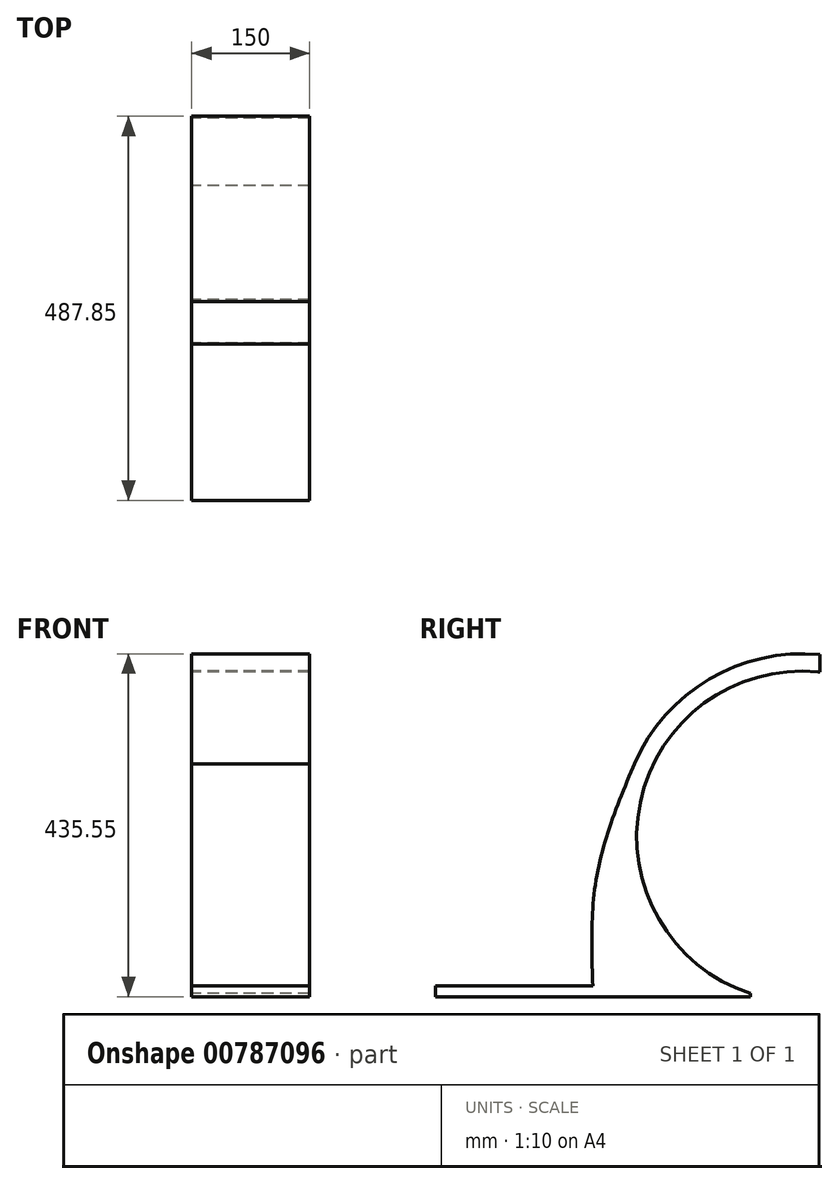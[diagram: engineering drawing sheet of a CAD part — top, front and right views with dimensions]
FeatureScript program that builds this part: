
annotation { "Feature Type Name" : "Feature", "Feature Type Description" : "" }
export const myFeature = defineFeature(function(context is Context, id is Id, definition is map)
    precondition{}
    {
        {
            var Q0;
            Q0=qCreatedBy(makeId("Right.planeOp"),FACE);
            var sketch = newSketch(context, id + "F0", { "sketchPlane" : qUnion([Q0])});
            skLineSegment(sketch, "E0", {"start": v(102.98, 0) * mm, "end": v(-97.02, 0) * mm});
            skLineSegment(sketch, "E1", {"start": v(-35.78, 150) * mm, "end": v(-92.34, 150) * mm});
            skPoint(sketch, "E2.third.point", {"position": v(169.6, 409.55) * mm});
            skArc(sketch, "E3", {"start": v(188.7, 408.56) * mm, "mid": v(-37.24, 242.69) * mm, "end": v(102.98, 0) * mm});
            skArc(sketch, "E4.0", {"start": v(190.83, 430.45) * mm, "mid": v(-52.22, 271.7) * mm, "end": v(50, 0) * mm});
            skFitSpline(sketch, "E5", {"points": [v(-97.02, 0) * mm, v(-92.34, 150) * mm, v(-44.67, 291.64) * mm], "startDerivative": vector(-12.28, 303.75) * mm, "endDerivative": vector(117.44, 279.34) * mm});
            skLineSegment(sketch, "E6", {"start": v(190.83, 430.45) * mm, "end": v(190.83, 408.56) * mm});
            skLineSegment(sketch, "E7", {"start": v(190.83, 408.56) * mm, "end": v(188.7, 408.56) * mm});
            skSolve(sketch);
        }
        {
            var Q0;
            {var subQ0=sQuery(id+"F0.wireOp",EDGE,"E5");var subQ1=sQuery(id+"F0.wireOp",EDGE,"E1");var subQ2=makeQuery(id+"F0.imprint","INTERSECT",VERTEX,{"derivedFrom":[subQ1,subQ0]});Q0=makeQuery(id+"F0.imprint","IMPRINT",FACE,{"disambiguationData":[TD([[makeQuery(id+"F0.imprint","IMPRINT",EDGE,{"disambiguationData":[TD([[subQ2,1.0]])],"derivedFrom":subQ1}),-1.0]])]});}
            var Q1;
            {var subQ0=sQuery(id+"F0.wireOp",EDGE,"E5");var subQ1=sQuery(id+"F0.wireOp",EDGE,"E0");var subQ2=makeQuery(id+"F0.imprint","INTERSECT",VERTEX,{"derivedFrom":[subQ1,subQ0]});Q1=makeQuery(id+"F0.imprint","IMPRINT",FACE,{"disambiguationData":[TD([[makeQuery(id+"F0.imprint","IMPRINT",EDGE,{"disambiguationData":[TD([[subQ2,1.0]])],"derivedFrom":subQ1}),-1.0]])]});}
            var Q2;
            {var subQ5=sQuery(id+"F0.wireOp",EDGE,"E6");Q2=makeQuery(id+"F0.imprint","IMPRINT",FACE,{"disambiguationData":[TD([[makeQuery(id+"F0.imprint","IMPRINT",EDGE,{"derivedFrom":subQ5}),-1.0]])]});}
            var Q3;
            {var subQ0=sQuery(id+"F0.wireOp",EDGE,"E3");var subQ1=sQuery(id+"F0.wireOp",EDGE,"E0");var subQ2=makeQuery(id+"F0.imprint","INTERSECT",VERTEX,{"derivedFrom":[subQ1,subQ0]});Q3=makeQuery(id+"F0.imprint","IMPRINT",FACE,{"disambiguationData":[TD([[makeQuery(id+"F0.imprint","IMPRINT",EDGE,{"disambiguationData":[TD([[subQ2,-1.0]])],"derivedFrom":subQ1}),-1.0]])]});}
            extrude(context, id + "F1", {"entities" : qUnion([Q0, Q1, Q2, Q3]), "endBound" : BoundingType.SYMMETRIC, "depth" : 150 * mm, "offsetDistance" : 25 * mm});
        }
        {
            var Q0;
            Q0=makeQuery(id+"F1.opExtrude","SWEPT_FACE",FACE,{"disambiguationData":[OSD([sQuery(id+"F0.wireOp",EDGE,"E0")])]});
            extrude(context, id + "F2", {"entities" : qUnion([Q0]), "operationType" : NewBodyOperationType.ADD, "depth" : 4 * mm, "offsetDistance" : 25 * mm});
        }
        {
            var Q0;
            Q0=makeQuery(id+"F2.opExtrude","SWEPT_FACE",FACE,{"disambiguationData":[OSD([sQuery(id+"F0.wireOp",EDGE,"E0"),sQuery(id+"F0.wireOp",EDGE,"E5")])]});
            extrude(context, id + "F3", {"entities" : qUnion([Q0]), "operationType" : NewBodyOperationType.ADD, "depth" : 200 * mm, "offsetDistance" : 25 * mm});
        }
        {
            var Q0;
            {var subQ0=sQuery(id+"F0.wireOp",EDGE,"E5");var subQ1=sQuery(id+"F0.wireOp",EDGE,"E0");Q0=makeQuery(id+"F3.opExtrude","SWEPT_FACE",FACE,{"disambiguationData":[OSD([subQ1,subQ0]),TDD([makeQuery(id+"F2.boolean.opBoolean","MERGE",EDGE,{"derivedFrom":[makeQuery(id+"F1.opExtrude","SWEPT_EDGE",EDGE,{"disambiguationData":[OSD([subQ1,subQ0])]}),makeQuery(id+"F2.opExtrude","CAP_EDGE",EDGE,{"disambiguationData":[OSD([subQ1,subQ0])],"isStart":true})]})])]});}
            extrude(context, id + "F4", {"entities" : qUnion([Q0]), "operationType" : NewBodyOperationType.ADD, "depth" : 10 * mm, "offsetDistance" : 25 * mm});
        }
    });
